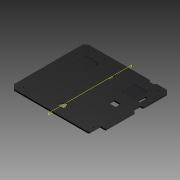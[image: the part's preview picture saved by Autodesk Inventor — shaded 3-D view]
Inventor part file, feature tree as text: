
AUTODESK INVENTOR PART (.ipt)
format: ipt  version: 2015 (Build 190159000, 159)  size: 414,208 bytes
history: native  units: mm
features: reference x76, extrude x10, hole x3, fillet x3, chamfer x1, pattern_linear x1, projected_geometry x1
ambient origin geometry x8: Origin, YZ Plane, XZ Plane, XY Plane, X Axis, Y Axis, Z Axis, Center Point
bodies: Solid1 (feature_tree)
feature tree (95):
  extrude  "Extrusión1"  Depth=480.0mm
  hole  "Agujero1"  [1 undecoded]
  extrude  "Extrusión11"  Depth=8.0mm TaperAngle=0.0deg
  extrude  "Extrusión13"  Depth=25.0mm
  fillet  "Empalme5"  Radius=36.0mm
  chamfer  "Chaflán5"  Distance=364.5mm
  hole  "Agujero2"  [1 undecoded]
  pattern_linear  "Patrón rectangular1"  Spacing1=10.0mm  [1 undecoded]
  hole  "Agujero3"  [1 undecoded]
  extrude  "Extrusión14"  Depth=31.5mm
  fillet  "Empalme7"  Radius=63.0mm
  extrude  "Extrusión15"  Depth=10.0mm TaperAngle=0.0deg
  extrude  "Extrusión17"  Depth=2.0mm
  extrude  "Extrusión18"  Depth=5.0mm TaperAngle=45.0deg
  extrude  "Extrusión19"  Depth=40.0mm
  fillet  "Empalme9"  Radius=30.0mm
  extrude  "Extrusión20"  Depth=170.5mm
  extrude  "Extrusión21"  Depth=150.0mm
  reference  "Referencia1"
  reference  "Referencia2"
  reference  "Referencia3"
  reference  "Referencia4"
  reference  "Referencia5"
  reference  "Referencia6"
  reference  "Referencia7"
  reference  "Referencia8"
  reference  "Referencia9"
  reference  "Referencia10"
  reference  "Referencia11"
  reference  "Referencia12"
  reference  "Referencia13"
  reference  "Referencia14"
  reference  "Referencia15"
  reference  "Referencia16"
  reference  "Referencia17"
  reference  "Referencia18"
  reference  "Referencia19"
  reference  "Referencia20"
  reference  "Referencia21"
  reference  "Referencia22"
  reference  "Referencia23"
  reference  "Referencia24"
  reference  "Referencia25"
  reference  "Referencia26"
  reference  "Referencia27"
  reference  "Referencia28"
  reference  "Referencia29"
  reference  "Referencia30"
  reference  "Referencia31"
  reference  "Referencia32"
  reference  "Referencia33"
  reference  "Referencia34"
  reference  "Referencia35"
  reference  "Referencia36"
  reference  "Referencia37"
  reference  "Referencia38"
  reference  "Referencia39"
  reference  "Referencia40"
  reference  "Referencia41"
  reference  "Referencia42"
  reference  "Referencia43"
  reference  "Referencia44"
  reference  "Referencia45"
  reference  "Referencia46"
  reference  "Referencia47"
  reference  "Referencia48"
  reference  "Referencia49"
  projected_geometry  "Contorno proyectado1"
  reference  "Referencia50"
  reference  "Referencia51"
  reference  "Referencia52"
  reference  "Referencia53"
  reference  "Referencia54"
  reference  "Referencia55"
  reference  "Referencia56"
  reference  "Referencia57"
  reference  "Referencia58"
  reference  "Referencia59"
  reference  "Referencia60"
  reference  "Referencia61"
  reference  "Referencia62"
  reference  "Referencia63"
  reference  "Referencia64"
  reference  "Referencia65"
  reference  "Referencia66"
  reference  "Referencia67"
  reference  "Referencia68"
  reference  "Referencia69"
  reference  "Referencia70"
  reference  "Referencia71"
  reference  "Referencia72"
  reference  "Referencia73"
  reference  "Referencia74"
  reference  "Referencia75"
  reference  "Referencia76"
note: 4 required parameter values undecoded (feature->parameter linkage not recoverable at this tier; creation-order binding heuristic only, values carry confidence <= 0.55)
